FCSTD DOCUMENT  (FreeCAD 1.0R38641 +468 (Git))
Label: AB25_assembly
License: All rights reserved
LicenseURL: https://en.wikipedia.org/wiki/All_rights_reserved
objects: App::Link×3, App::FeaturePython×1, Assembly::JointGroup×1, Assembly::AssemblyObject×1
EXTERNAL_REF file=00_pulley_holder_screw.FCStd obj=Body
EXTERNAL_REF file=02nema23_bracket_offsettirroir.FCStd obj=Body
EXTERNAL_REF file=00GT5belt_fix_m5insert.FCStd obj=Body

FEATURE [App::Link] Body
  LinkedObject = -> <external 00_pulley_holder_screw.FCStd>#Body
FEATURE [App::FeaturePython] GroundedJoint  # Assembly grounded joint (typed FeaturePython)
  ObjectToGround = -> Body
FEATURE [Assembly::JointGroup] Joints
  Group = -> [GroundedJoint]
FEATURE [App::Link] Body001
  LinkPlacement = pos=(-215,25,36.0435) rot=(0,0,1;0rad)
  LinkedObject = -> <external 02nema23_bracket_offsettirroir.FCStd>#Body
  Placement = pos=(-215,25,36.0435) rot=(0,0,1;0rad)
FEATURE [App::Link] Body002
  LinkPlacement = pos=(-100.942,-12.8294,76.5401) rot=(0.582997,0.582996,-0.582997;4.18879rad)
  LinkedObject = -> <external 00GT5belt_fix_m5insert.FCStd>#Body
  Placement = pos=(-100.942,-12.8294,76.5401) rot=(0.582997,0.582996,-0.582997;4.18879rad)
FEATURE [Assembly::AssemblyObject] Assembly
  Group = -> [Joints,Body,GroundedJoint,Body001,Body002]
  Origin = -> Origin
  Type = Assembly

RESOLVED EXTERNAL PARTS (link-assembly join: the EXTERNAL_REF files above that resolve inside this repo's crawl, each included once):
---- part 00GT5belt_fix_m5insert.FCStd = doc fcstd_30b9b50c09c9 ----
FCSTD DOCUMENT  (FreeCAD 1.0R38641 +468 (Git))
Label: 00GT5belt_fix_m5insert
License: All rights reserved
LicenseURL: https://en.wikipedia.org/wiki/All_rights_reserved
objects: Sketcher::SketchObject×3, PartDesign::Pocket×2, PartDesign::Fillet×2, PartDesign::Pad×1, PartDesign::Plane×1, PartDesign::Mirrored×1, PartDesign::Body×1
note: 25 computed .brp shape members not serialized (recipe doc carries the construction recipe); baked Part::Feature solids carry a one-line shape summary decoded from their .brp

FEATURE [Sketcher::SketchObject] Sketch
  ArcFitTolerance = 1e-06
  AttachmentSupport = -> [XZ_Plane]
  FullyConstrained = true
  MakeInternals = false
  MapMode = 5
  Placement = pos=(0,0,0) rot=(1,0,0;1.5708rad)
  sketch-geometry (11):
    g0: LineSegment StartX=-14 StartY=-8.75 StartZ=0 EndX=14 EndY=-8.75 EndZ=0
    g1: LineSegment StartX=14 StartY=-8.75 StartZ=0 EndX=14 EndY=8.75 EndZ=0
    g2: LineSegment StartX=14 StartY=8.75 StartZ=0 EndX=-14 EndY=8.75 EndZ=0
    g3: LineSegment StartX=-14 StartY=8.75 StartZ=0 EndX=-14 EndY=-8.75 EndZ=0
    g4: GeomPoint [constr] X=0 Y=0 Z=0
    g5: GeomPoint [constr] X=0 Y=0 Z=0
    g6: LineSegment StartX=-6.5 StartY=-5.75 StartZ=0 EndX=6.5 EndY=-5.75 EndZ=0
    g7: LineSegment StartX=6.5 StartY=-5.75 StartZ=0 EndX=6.5 EndY=-0.75 EndZ=0
    g8: LineSegment StartX=6.5 StartY=-0.75 StartZ=0 EndX=-6.5 EndY=-0.75 EndZ=0
    g9: LineSegment StartX=-6.5 StartY=-0.75 StartZ=0 EndX=-6.5 EndY=-5.75 EndZ=0
    g10: GeomPoint [constr] X=0 Y=-3.25 Z=0
  constraints (27):
    c: Coincident(g0,g1)
    c: Coincident(g1,g2)
    c: Coincident(g2,g3)
    c: Coincident(g3,g0)
    c: Horizontal(g0)
    c: Horizontal(g2)
    c: Vertical(g1)
    c: Vertical(g3)
    c: Symmetric(g2,g0,g4)
    c: Distance(g1,g3) = 28
    c: Distance(g0,g2) = 17.5
    c: Coincident(g4,g-1)
    c: Coincident(g5,g4)
    c: Coincident(g6,g7)
    c: Coincident(g7,g8)
    c: Coincident(g8,g9)
    c: Coincident(g9,g6)
    c: Horizontal(g6)
    c: Horizontal(g8)
    c: Vertical(g7)
    c: Vertical(g9)
    c: Symmetric(g8,g6,g10)
    c: Distance(g7,g9) = 13
    c: Distance(g6,g8) = 5
    c: PointOnObject(g10,g-2)
    c: DistanceY(g0,g6) = 3
    c: DistanceY(g7,g1) = 9.5
FEATURE [PartDesign::Pad] Pad
  Direction = (0,-1,2e-16)
  Length = 30
  Length2 = 10
  Placement = pos=(0,0,0) rot=(1,0,0;1.5708rad)
  Profile = -> Sketch
  ReferenceAxis = -> Sketch [N_Axis]
  Refine = true
  Suppressed = false
  Type = 0
FEATURE [PartDesign::Plane] DatumPlane
  AttachmentSupport = -> [Pad]
  Length = 60.4881
  MapMode = 5
  Placement = pos=(0,1.9e-15,8.75) rot=(0,0,1;3.14159rad)
  ResizeMode = 0
  Width = 65.4881
FEATURE [Sketcher::SketchObject] Sketch001
  ArcFitTolerance = 1e-06
  AttachmentSupport = -> [DatumPlane]
  ExternalGeometry = -> [Pad]
  FullyConstrained = false
  MakeInternals = false
  MapMode = 5
  Placement = pos=(0,1.9e-15,8.75) rot=(0,0,1;3.14159rad)
  sketch-geometry (3):
    g0: Circle CenterX=9e-16 CenterY=15 CenterZ=0 NormalX=0 NormalY=0 NormalZ=1 AngleXU=0 Radius=3.55
    g1: Circle CenterX=9 CenterY=25 CenterZ=0 NormalX=0 NormalY=0 NormalZ=1 AngleXU=0 Radius=1.0752
    g2: Circle CenterX=9 CenterY=5 CenterZ=0 NormalX=0 NormalY=0 NormalZ=1 AngleXU=0 Radius=1.08784
  constraints (5):
    c: Diameter(g0) = 7.1
    c: Vertical(g2,g1)
    c: DistanceX(g1,g-3) = 5
    c: DistanceY(g1,g-3) = 5
    c: DistanceY(g-3,g2) = 5
FEATURE [PartDesign::Pocket] Pocket
  BaseFeature = -> Pad
  Direction = (0,0,-1)
  Length = 5
  Length2 = 5
  Placement = pos=(0,0,0) rot=(1,0,0;1.5708rad)
  Profile = -> Sketch001
  ReferenceAxis = -> Sketch001 [N_Axis]
  Refine = true
  Suppressed = false
  Type = 1
FEATURE [PartDesign::Mirrored] Mirrored
  BaseFeature = -> Pocket
  MirrorPlane = -> Sketch001 [V_Axis]
  Originals = -> [Pocket]
  Placement = pos=(0,0,0) rot=(1,0,0;1.5708rad)
  Refine = true
  Suppressed = false
  TransformMode = 0
FEATURE [Sketcher::SketchObject] Sketch002
  ArcFitTolerance = 1e-06
  AttachmentSupport = -> [Mirrored]
  ExternalGeometry = -> [Mirrored]
  FullyConstrained = true
  MakeInternals = false
  MapMode = 5
  Placement = pos=(0,-1.9e-15,-8.75) rot=(1,0,0;3.14159rad)
  sketch-geometry (5):
    g0: LineSegment StartX=-6.5 StartY=11.25 StartZ=0 EndX=6.5 EndY=11.25 EndZ=0
    g1: LineSegment StartX=6.5 StartY=11.25 StartZ=0 EndX=6.5 EndY=18.75 EndZ=0
    g2: LineSegment StartX=6.5 StartY=18.75 StartZ=0 EndX=-6.5 EndY=18.75 EndZ=0
    g3: LineSegment StartX=-6.5 StartY=18.75 StartZ=0 EndX=-6.5 EndY=11.25 EndZ=0
    g4: GeomPoint [constr] X=0 Y=15 Z=0
  constraints (12):
    c: Coincident(g0,g1)
    c: Coincident(g1,g2)
    c: Coincident(g2,g3)
    c: Coincident(g3,g0)
    c: Horizontal(g0)
    c: Horizontal(g2)
    c: Vertical(g1)
    c: Vertical(g3)
    c: Symmetric(g2,g0,g4)
    c: Distance(g1,g3) = 13
    c: Distance(g0,g2) = 7.5
    c: Coincident(g4,g-3)
FEATURE [PartDesign::Pocket] Pocket001
  BaseFeature = -> Mirrored
  Direction = (0,0,1)
  Length = 5
  Length2 = 5
  Placement = pos=(0,0,0) rot=(1,0,0;1.5708rad)
  Profile = -> Sketch002
  ReferenceAxis = -> Sketch002 [N_Axis]
  Refine = true
  Suppressed = false
  Type = 0
FEATURE [PartDesign::Fillet] Fillet
  Base = -> Pocket001 [Face2,Face5,Face3,Edge22,Edge15,Edge23]
  BaseFeature = -> Pocket001
  Placement = pos=(0,0,0) rot=(1,0,0;1.5708rad)
  Radius = 1
  Refine = true
  SupportTransform = false
  Suppressed = false
  UseAllEdges = false
FEATURE [PartDesign::Fillet] Fillet001
  Base = -> Fillet [Edge16]
  BaseFeature = -> Fillet
  Placement = pos=(0,0,0) rot=(1,0,0;1.5708rad)
  Radius = 2
  Refine = true
  SupportTransform = false
  Suppressed = false
  UseAllEdges = false
FEATURE [PartDesign::Body] Body
  AllowCompound = false
  Group = -> [Sketch,Pad,DatumPlane,Sketch001,Pocket,Mirrored,Sketch002,Pocket001,Fillet,Fillet001]
  Origin = -> Origin
  Tip = -> Fillet001
---- part 00_pulley_holder_screw.FCStd = doc fcstd_3f0da93ca95a ----
FCSTD DOCUMENT  (FreeCAD 1.0R38641 +468 (Git))
Label: 00_pulley_holder_screw
License: All rights reserved
LicenseURL: https://en.wikipedia.org/wiki/All_rights_reserved
objects: Sketcher::SketchObject×4, PartDesign::Fillet×4, PartDesign::Plane×2, PartDesign::Pocket×2, PartDesign::Pad×1, PartDesign::Hole×1, PartDesign::Body×1
note: 35 computed .brp shape members not serialized (recipe doc carries the construction recipe); baked Part::Feature solids carry a one-line shape summary decoded from their .brp

FEATURE [Sketcher::SketchObject] Sketch
  ArcFitTolerance = 1e-06
  AttachmentSupport = -> [XZ_Plane]
  FullyConstrained = true
  MakeInternals = false
  MapMode = 5
  Placement = pos=(0,0,0) rot=(1,0,0;1.5708rad)
  sketch-geometry (13):
    g0: LineSegment StartX=-20 StartY=0 StartZ=0 EndX=20 EndY=0 EndZ=0
    g1: LineSegment [constr] StartX=20 StartY=0 StartZ=0 EndX=10 EndY=50 EndZ=0
    g2: LineSegment [constr] StartX=10 StartY=50 StartZ=0 EndX=-10 EndY=50 EndZ=0
    g3: LineSegment [constr] StartX=-10 StartY=50 StartZ=0 EndX=-20 EndY=0 EndZ=0
    g4: Circle [constr] CenterX=-7e-16 CenterY=50 CenterZ=0 NormalX=0 NormalY=0 NormalZ=1 AngleXU=0 Radius=10
    g5: LineSegment [constr] StartX=0 StartY=60 StartZ=0 EndX=0 EndY=0 EndZ=0
    g6: ArcOfCircle CenterX=-7e-16 CenterY=50 CenterZ=0 NormalX=0 NormalY=0 NormalZ=1 AngleXU=0 Radius=10 StartAngle=0 EndAngle=3.14159
    g7: LineSegment StartX=-20 StartY=0 StartZ=0 EndX=-20 EndY=10 EndZ=0
    g8: LineSegment StartX=-20 StartY=10 StartZ=0 EndX=-10 EndY=10 EndZ=0
    g9: LineSegment StartX=-10 StartY=10 StartZ=0 EndX=-10 EndY=50 EndZ=0
    g10: LineSegment StartX=10 StartY=50 StartZ=0 EndX=10 EndY=10 EndZ=0
    g11: LineSegment StartX=10 StartY=10 StartZ=0 EndX=20 EndY=10 EndZ=0
    g12: LineSegment StartX=20 StartY=10 StartZ=0 EndX=20 EndY=0 EndZ=0
  constraints (34):
    c: PointOnObject(g0,g-1)
    c: Coincident(g0,g1)
    c: Coincident(g1,g2)
    c: Coincident(g2,g3)
    c: Coincident(g3,g0)
    c: Symmetric(g1,g2,g-2)
    c: Symmetric(g0,g0,g-2)
    c: Symmetric(g2,g2,g4)
    c: Diameter(g4) = 20
    c: PointOnObject(g5,g4)
    c: PointOnObject(g5,g0)
    c: Vertical(g5)
    c: PointOnObject(g5,g-2)
    c: DistanceY(g5,g5) = 60
    c: PointOnObject(g2,g4)
    c: Coincident(g6,g4)
    c: Coincident(g6,g2)
    c: Coincident(g6,g1)
    c: Coincident(g0,g7)
    c: Vertical(g7)
    c: Coincident(g7,g8)
    c: Horizontal(g8)
    c: Coincident(g8,g9)
    c: Coincident(g9,g2)
    c: Coincident(g1,g10)
    c: Coincident(g10,g11)
    c: Coincident(g11,g12)
    c: Coincident(g12,g0)
    c: Horizontal(g11)
    c: Vertical(g12)
    c: Vertical(g10)
    c: Symmetric(g8,g10,g5)
    c: DistanceX(g0,g0) = 40
    c: DistanceY(g12,g12) = 10
FEATURE [PartDesign::Pad] Pad
  Direction = (0,-1,2e-16)
  Length = 30
  Length2 = 10
  Placement = pos=(0,0,0) rot=(1,0,0;1.5708rad)
  Profile = -> Sketch
  ReferenceAxis = -> Sketch [N_Axis]
  Refine = true
  Suppressed = false
  Type = 0
FEATURE [PartDesign::Plane] DatumPlane
  AttachmentOffset = pos=(0,0,-15) rot=(0,0,1;0rad)
  AttachmentSupport = -> [Pad]
  Length = 60
  MapMode = 5
  Placement = pos=(0,-15,-3.3e-15) rot=(-1,0,0;1.5708rad)
  ResizeMode = 0
  Width = 60
FEATURE [Sketcher::SketchObject] Sketch001
  ArcFitTolerance = 1e-06
  AttachmentSupport = -> [DatumPlane]
  FullyConstrained = false
  MakeInternals = false
  MapMode = 5
  Placement = pos=(0,-15,-3.3e-15) rot=(-1,0,0;1.5708rad)
  sketch-geometry (4):
    g0: LineSegment StartX=-20.8879 StartY=-62.8901 StartZ=0 EndX=20.8879 EndY=-62.8901 EndZ=0
    g1: LineSegment StartX=20.8879 StartY=-62.8901 StartZ=0 EndX=20.8879 EndY=-37.1099 EndZ=0
    g2: LineSegment StartX=20.8879 StartY=-37.1099 StartZ=0 EndX=-20.8879 EndY=-37.1099 EndZ=0
    g3: LineSegment StartX=-20.8879 StartY=-37.1099 StartZ=0 EndX=-20.8879 EndY=-62.8901 EndZ=0
  constraints (8):
    c: Coincident(g0,g1)
    c: Coincident(g1,g2)
    c: Coincident(g2,g3)
    c: Coincident(g3,g0)
    c: Horizontal(g0)
    c: Horizontal(g2)
    c: Vertical(g1)
    c: Vertical(g3)
FEATURE [PartDesign::Pocket] Pocket
  BaseFeature = -> Pad
  Direction = (0,-1,-2e-16)
  Length = 16.7
  Length2 = 5
  Midplane = true
  Placement = pos=(0,0,0) rot=(1,0,0;1.5708rad)
  Profile = -> Sketch001
  ReferenceAxis = -> Sketch001 [N_Axis]
  Refine = true
  Suppressed = false
  Type = 0
FEATURE [Sketcher::SketchObject] Sketch002
  ArcFitTolerance = 1e-06
  AttachmentSupport = -> [Pocket]
  ExternalGeometry = -> [Pocket]
  FullyConstrained = true
  MakeInternals = false
  MapMode = 5
  Placement = pos=(0,5.1e-15,0) rot=(-1,0,0;1.5708rad)
  sketch-geometry (1):
    g0: Circle CenterX=0 CenterY=-50 CenterZ=0 NormalX=0 NormalY=0 NormalZ=1 AngleXU=0 Radius=2.75
  constraints (2):
    c: Coincident(g0,g-3)
    c: Diameter(g0) = 5.5
FEATURE [PartDesign::Pocket] Pocket001
  BaseFeature = -> Pocket
  Direction = (0,-1,-2e-16)
  Length = 5
  Length2 = 5
  Placement = pos=(0,0,0) rot=(1,0,0;1.5708rad)
  Profile = -> Sketch002
  ReferenceAxis = -> Sketch002 [N_Axis]
  Refine = true
  Suppressed = false
  Type = 1
FEATURE [PartDesign::Plane] DatumPlane001
  AttachmentOffset = pos=(0,0,-16) rot=(0,0,1;0rad)
  AttachmentSupport = -> [Pocket001]
  Length = 60
  MapMode = 5
  Placement = pos=(0,0,16) rot=(1,0,0;3.14159rad)
  ResizeMode = 0
  Width = 60
FEATURE [Sketcher::SketchObject] Sketch003
  ArcFitTolerance = 1e-06
  AttachmentSupport = -> [DatumPlane001]
  ExternalGeometry = -> [Pocket001]
  FullyConstrained = false
  MakeInternals = false
  MapMode = 5
  Placement = pos=(0,0,16) rot=(1,0,0;3.14159rad)
  sketch-geometry (11):
    g0: Circle [constr] CenterX=15 CenterY=15 CenterZ=0 NormalX=0 NormalY=0 NormalZ=1 AngleXU=0 Radius=1.16725
    g1: LineSegment [constr] StartX=10 StartY=30 StartZ=0 EndX=10 EndY=0 EndZ=0
    g2: ArcOfCircle CenterX=15 CenterY=25 CenterZ=0 NormalX=0 NormalY=0 NormalZ=1 AngleXU=0 Radius=1.5 StartAngle=4e-16 EndAngle=3.14159
    g3: ArcOfCircle CenterX=15 CenterY=5 CenterZ=0 NormalX=0 NormalY=0 NormalZ=1 AngleXU=0 Radius=1.5 StartAngle=3.14159 EndAngle=6.28319
    g4: LineSegment StartX=16.5 StartY=25 StartZ=0 EndX=16.5 EndY=5 EndZ=0
    g5: LineSegment StartX=13.5 StartY=25 StartZ=0 EndX=13.5 EndY=5 EndZ=0
    g6: Circle [constr] CenterX=-15 CenterY=15 CenterZ=0 NormalX=0 NormalY=0 NormalZ=1 AngleXU=0 Radius=1.16725
    g7: ArcOfCircle CenterX=-15 CenterY=25 CenterZ=0 NormalX=0 NormalY=0 NormalZ=1 AngleXU=0 Radius=1.5 StartAngle=1e-16 EndAngle=3.14159
    g8: ArcOfCircle CenterX=-15 CenterY=5 CenterZ=0 NormalX=0 NormalY=0 NormalZ=1 AngleXU=0 Radius=1.5 StartAngle=3.14159 EndAngle=6.28319
    g9: LineSegment StartX=-13.5 StartY=25 StartZ=0 EndX=-13.5 EndY=5 EndZ=0
    g10: LineSegment StartX=-16.5 StartY=25 StartZ=0 EndX=-16.5 EndY=5 EndZ=0
  constraints (23):
    c: Vertical(g1)
    c: Horizontal(g1,g-3)
    c: Horizontal(g1,g-3)
    c: Symmetric(g-3,g1,g0)
    c: PointOnObject(g-5,g1)
    c: Tangent(g2,g4) = 1.5708
    c: Tangent(g2,g5) = -1.5708
    c: Tangent(g3,g4) = 1.5708
    c: Tangent(g3,g5) = -1.5708
    c: Equal(g2,g3)
    c: Vertical(g4)
    c: Radius(g2) = 1.5
    c: Symmetric(g2,g3,g0)
    c: DistanceY(g3,g2) = 20
    c: Tangent(g7,g9) = 1.5708
    c: Tangent(g7,g10) = -1.5708
    c: Tangent(g8,g9) = 1.5708
    c: Tangent(g8,g10) = -1.5708
    c: Equal(g7,g8)
    c: Vertical(g9)
    c: Radius(g7) = 1.5
    c: Symmetric(g7,g8,g6)
    c: DistanceY(g8,g7) = 20
FEATURE [PartDesign::Fillet] Fillet
  Base = -> Pocket001 [Edge26,Edge34]
  BaseFeature = -> Pocket001
  Placement = pos=(0,0,0) rot=(1,0,0;1.5708rad)
  Radius = 7
  Refine = true
  SupportTransform = false
  Suppressed = false
  UseAllEdges = false
FEATURE [PartDesign::Fillet] Fillet001
  Base = -> Fillet [Edge47,Edge8]
  BaseFeature = -> Fillet
  Placement = pos=(0,0,0) rot=(1,0,0;1.5708rad)
  Radius = 8
  Refine = true
  SupportTransform = false
  Suppressed = false
  UseAllEdges = false
FEATURE [PartDesign::Fillet] Fillet002
  Base = -> Fillet001 [Edge49,Edge52]
  BaseFeature = -> Fillet001
  Placement = pos=(0,0,0) rot=(1,0,0;1.5708rad)
  Radius = 1
  Refine = true
  SupportTransform = false
  Suppressed = false
  UseAllEdges = false
FEATURE [PartDesign::Hole] Hole
  BaseFeature = -> Fillet002
  CustomThreadClearance = 0
  Depth = 157.654
  DepthType = 1
  Diameter = 3
  DrillForDepth = false
  DrillPoint = 1
  DrillPointAngle = 118
  HoleCutCountersinkAngle = 90
  HoleCutCustomValues = false
  HoleCutDepth = 6.1
  HoleCutDiameter = 5
  HoleCutType = 3
  ModelThread = false
  Placement = pos=(0,0,0) rot=(1,0,0;1.5708rad)
  Profile = -> Sketch003
  Refine = true
  Reversed = true
  Suppressed = false
  Tapered = false
  TaperedAngle = 90
  ThreadClass = 0
  ThreadDepth = 157.654
  ThreadDepthType = 0
  ThreadDirection = 0
  ThreadFit = 0
  ThreadSize = 0
  ThreadType = 0
  Threaded = false
  UseCustomThreadClearance = false
FEATURE [PartDesign::Fillet] Fillet003
  Base = -> Hole [Edge46,Edge30,Edge48,Edge27]
  BaseFeature = -> Hole
  Placement = pos=(0,0,0) rot=(1,0,0;1.5708rad)
  Radius = 1
  Refine = true
  SupportTransform = false
  Suppressed = false
  UseAllEdges = false
FEATURE [PartDesign::Body] Body
  AllowCompound = false
  Group = -> [Sketch,Pad,DatumPlane,Sketch001,Pocket,Sketch002,Pocket001,DatumPlane001,Sketch003,Fillet,Fillet001,Fillet002,Hole,Fillet003]
  Origin = -> Origin
  Tip = -> Fillet003
---- part 02nema23_bracket_offsettirroir.FCStd = doc fcstd_2a5d42de8e11 ----
FCSTD DOCUMENT  (FreeCAD 1.0R38641 +468 (Git))
Label: 02nema23_bracket_offsettirroir
License: All rights reserved
LicenseURL: https://en.wikipedia.org/wiki/All_rights_reserved
objects: Sketcher::SketchObject×3, PartDesign::Pocket×2, PartDesign::Fillet×2, PartDesign::Chamfer×2, PartDesign::Pad×1, PartDesign::Mirrored×1, PartDesign::Body×1
note: 30 computed .brp shape members not serialized (recipe doc carries the construction recipe); baked Part::Feature solids carry a one-line shape summary decoded from their .brp

FEATURE [Sketcher::SketchObject] Sketch
  ArcFitTolerance = 1e-06
  AttachmentSupport = -> [XZ_Plane]
  FullyConstrained = false
  MakeInternals = false
  MapMode = 5
  Placement = pos=(0,0,0) rot=(1,0,0;1.5708rad)
  sketch-geometry (17):
    g0: Circle CenterX=-23.57 CenterY=-23.57 CenterZ=0 NormalX=0 NormalY=0 NormalZ=1 AngleXU=0 Radius=2.8
    g1: Circle CenterX=23.57 CenterY=-23.57 CenterZ=0 NormalX=0 NormalY=0 NormalZ=1 AngleXU=0 Radius=2.8
    g2: Circle CenterX=-23.57 CenterY=23.57 CenterZ=0 NormalX=0 NormalY=0 NormalZ=1 AngleXU=0 Radius=2.8
    g3: Circle CenterX=0 CenterY=0 CenterZ=0 NormalX=0 NormalY=0 NormalZ=1 AngleXU=0 Radius=19.9145
    g4: Circle CenterX=23.57 CenterY=23.57 CenterZ=0 NormalX=0 NormalY=0 NormalZ=1 AngleXU=0 Radius=2.8
    g5: Circle [constr] CenterX=0 CenterY=0 CenterZ=0 NormalX=0 NormalY=0 NormalZ=1 AngleXU=0 Radius=22
    g6: LineSegment [constr] StartX=0 StartY=22 StartZ=0 EndX=0 EndY=-38 EndZ=0
    g7: LineSegment StartX=33 StartY=-18 StartZ=0 EndX=33 EndY=29 EndZ=0
    g8: LineSegment StartX=33 StartY=29 StartZ=0 EndX=-33 EndY=29 EndZ=0
    g9: LineSegment StartX=-33 StartY=29 StartZ=0 EndX=-33 EndY=-18 EndZ=0
    g10: LineSegment [constr] StartX=-33 StartY=-18 StartZ=0 EndX=33 EndY=-18 EndZ=0
    g11: GeomPoint [constr] X=0 Y=0 Z=0
    g12: LineSegment StartX=-33 StartY=-18 StartZ=0 EndX=-63 EndY=-18 EndZ=0
    g13: LineSegment StartX=-63 StartY=-18 StartZ=0 EndX=-63 EndY=-38 EndZ=0
    g14: LineSegment StartX=-63 StartY=-38 StartZ=0 EndX=63 EndY=-38 EndZ=0
    g15: LineSegment StartX=63 StartY=-38 StartZ=0 EndX=63 EndY=-18 EndZ=0
    g16: LineSegment StartX=63 StartY=-18 StartZ=0 EndX=33 EndY=-18 EndZ=0
  constraints (34):
    c: Diameter(g5) = 44
    c: Coincident(g5,g3)
    c: PointOnObject(g6,g5)
    c: Vertical(g6)
    c: DistanceY(g6,g6) = 60
    c: Coincident(g3,g-1)
    c: PointOnObject(g6,g-2)
    c: Coincident(g7,g8)
    c: Coincident(g8,g9)
    c: Coincident(g9,g10)
    c: Coincident(g10,g7)
    c: Vertical(g7)
    c: Vertical(g9)
    c: Horizontal(g8)
    c: Horizontal(g10)
    c: Coincident(g11,g3)
    c: Horizontal(g12)
    c: Coincident(g12,g13)
    c: Coincident(g13,g14)
    c: Coincident(g14,g15)
    c: Coincident(g15,g16)
    c: Vertical(g15)
    c: Vertical(g13)
    c: Horizontal(g16)
    c: PointOnObject(g6,g14)
    c: Coincident(g9,g12)
    c: Coincident(g7,g16)
    c: Symmetric(g13,g14,g-2)
    c: Diameter(g0) = 5.6
    c: DistanceX(g8,g8) = 66
    c: Equal(g12,g16)
    c: DistanceX(g16,g16) = 30
    c: DistanceY(g3,g7) = 29
    c: DistanceY(g15,g15) = 20
FEATURE [PartDesign::Pad] Pad
  Direction = (0,-1,2e-16)
  Length = 20
  Length2 = 10
  Placement = pos=(0,0,0) rot=(1,0,0;1.5708rad)
  Profile = -> Sketch
  ReferenceAxis = -> Sketch [N_Axis]
  Refine = true
  Suppressed = false
  Type = 0
FEATURE [Sketcher::SketchObject] Sketch001
  ArcFitTolerance = 1e-06
  AttachmentSupport = -> [Pad]
  ExternalGeometry = -> [Pad]
  FullyConstrained = true
  MakeInternals = false
  MapMode = 5
  Placement = pos=(0,-1.9e-15,0) rot=(-1,0,0;1.5708rad)
  sketch-geometry (5):
    g0: LineSegment StartX=28.75 StartY=29 StartZ=0 EndX=-28.75 EndY=29 EndZ=0
    g1: LineSegment StartX=-28.75 StartY=29 StartZ=0 EndX=-28.75 EndY=-29 EndZ=0
    g2: LineSegment StartX=-28.75 StartY=-29 StartZ=0 EndX=28.75 EndY=-29 EndZ=0
    g3: LineSegment StartX=28.75 StartY=-29 StartZ=0 EndX=28.75 EndY=29 EndZ=0
    g4: GeomPoint [constr] X=0 Y=0 Z=0
  constraints (12):
    c: Coincident(g0,g1)
    c: Coincident(g1,g2)
    c: Coincident(g2,g3)
    c: Coincident(g3,g0)
    c: Horizontal(g0)
    c: Horizontal(g2)
    c: Vertical(g1)
    c: Vertical(g3)
    c: Symmetric(g2,g0,g4)
    c: Coincident(g4,g-1)
    c: PointOnObject(g1,g-4)
    c: DistanceX(g2,g2) = 57.5
FEATURE [PartDesign::Pocket] Pocket
  BaseFeature = -> Pad
  Direction = (0,-1,-2e-16)
  Length = 12
  Length2 = 5
  Placement = pos=(0,0,0) rot=(1,0,0;1.5708rad)
  Profile = -> Sketch001
  ReferenceAxis = -> Sketch001 [N_Axis]
  Refine = true
  Suppressed = false
  Type = 0
FEATURE [Sketcher::SketchObject] Sketch002
  ArcFitTolerance = 1e-06
  AttachmentSupport = -> [Pocket]
  ExternalGeometry = -> [Pocket]
  FullyConstrained = false
  MakeInternals = false
  MapMode = 5
  Placement = pos=(0,-7.9e-15,-18) rot=(0,0,1;3.14159rad)
  sketch-geometry (5):
    g0: LineSegment [constr] StartX=-62.9994 StartY=10 StartZ=0 EndX=101.936 EndY=10 EndZ=0
    g1: ArcOfCircle CenterX=-55.5 CenterY=10 CenterZ=0 NormalX=0 NormalY=0 NormalZ=1 AngleXU=0 Radius=2.5 StartAngle=1.5708 EndAngle=4.71239
    g2: ArcOfCircle CenterX=-40.5 CenterY=10 CenterZ=0 NormalX=0 NormalY=0 NormalZ=1 AngleXU=0 Radius=2.5 StartAngle=4.71239 EndAngle=7.85398
    g3: LineSegment StartX=-55.5 StartY=12.5 StartZ=0 EndX=-40.5 EndY=12.5 EndZ=0
    g4: LineSegment StartX=-55.5 StartY=7.5 StartZ=0 EndX=-40.5 EndY=7.5 EndZ=0
  constraints (11):
    c: Symmetric(g-3,g-4,g0)
    c: Tangent(g1,g3) = 1.5708
    c: Tangent(g1,g4) = -1.5708
    c: Tangent(g2,g3) = 1.5708
    c: Tangent(g2,g4) = -1.5708
    c: Equal(g1,g2)
    c: Horizontal(g4)
    c: PointOnObject(g1,g0)
    c: Radius(g2) = 2.5
    c: DistanceX(g-3,g1) = 7.5
    c: DistanceX(g2,g-3) = 7.5
FEATURE [PartDesign::Pocket] Pocket001
  BaseFeature = -> Pocket
  Direction = (0,0,-1)
  Length = 5
  Length2 = 5
  Placement = pos=(0,0,0) rot=(1,0,0;1.5708rad)
  Profile = -> Sketch002
  ReferenceAxis = -> Sketch002 [N_Axis]
  Refine = true
  Suppressed = false
  Type = 1
FEATURE [PartDesign::Mirrored] Mirrored
  BaseFeature = -> Pocket001
  MirrorPlane = -> Sketch002 [V_Axis]
  Originals = -> [Pocket001]
  Placement = pos=(0,0,0) rot=(1,0,0;1.5708rad)
  Refine = true
  Suppressed = false
  TransformMode = 0
FEATURE [PartDesign::Fillet] Fillet
  Base = -> Mirrored [Edge1,Edge56]
  BaseFeature = -> Mirrored
  Placement = pos=(0,0,0) rot=(1,0,0;1.5708rad)
  Radius = 4
  Refine = true
  SupportTransform = false
  Suppressed = false
  UseAllEdges = false
FEATURE [PartDesign::Fillet] Fillet001
  Base = -> Fillet [Edge1,Edge16,Edge4,Edge26,Edge37,Edge57,Edge13,Edge31,Edge9,Edge27]
  BaseFeature = -> Fillet
  Placement = pos=(0,0,0) rot=(1,0,0;1.5708rad)
  Radius = 1
  Refine = true
  SupportTransform = false
  Suppressed = false
  UseAllEdges = false
FEATURE [PartDesign::Chamfer] Chamfer
  Angle = 45
  Base = -> Fillet001 [Edge56,Edge65]
  BaseFeature = -> Fillet001
  ChamferType = 0
  FlipDirection = false
  Placement = pos=(0,0,0) rot=(1,0,0;1.5708rad)
  Refine = true
  Size = 1
  Size2 = 1
  SupportTransform = false
  Suppressed = false
  UseAllEdges = false
FEATURE [PartDesign::Chamfer] Chamfer001
  Angle = 45
  Base = -> Chamfer [Edge70]
  BaseFeature = -> Chamfer
  ChamferType = 0
  FlipDirection = false
  Placement = pos=(0,0,0) rot=(1,0,0;1.5708rad)
  Refine = true
  Size = 1
  Size2 = 1
  SupportTransform = false
  Suppressed = false
  UseAllEdges = false
FEATURE [PartDesign::Body] Body
  AllowCompound = false
  Group = -> [Sketch,Pad,Sketch001,Pocket,Sketch002,Pocket001,Mirrored,Fillet,Fillet001,Chamfer,Chamfer001]
  Origin = -> Origin
  Tip = -> Chamfer001
